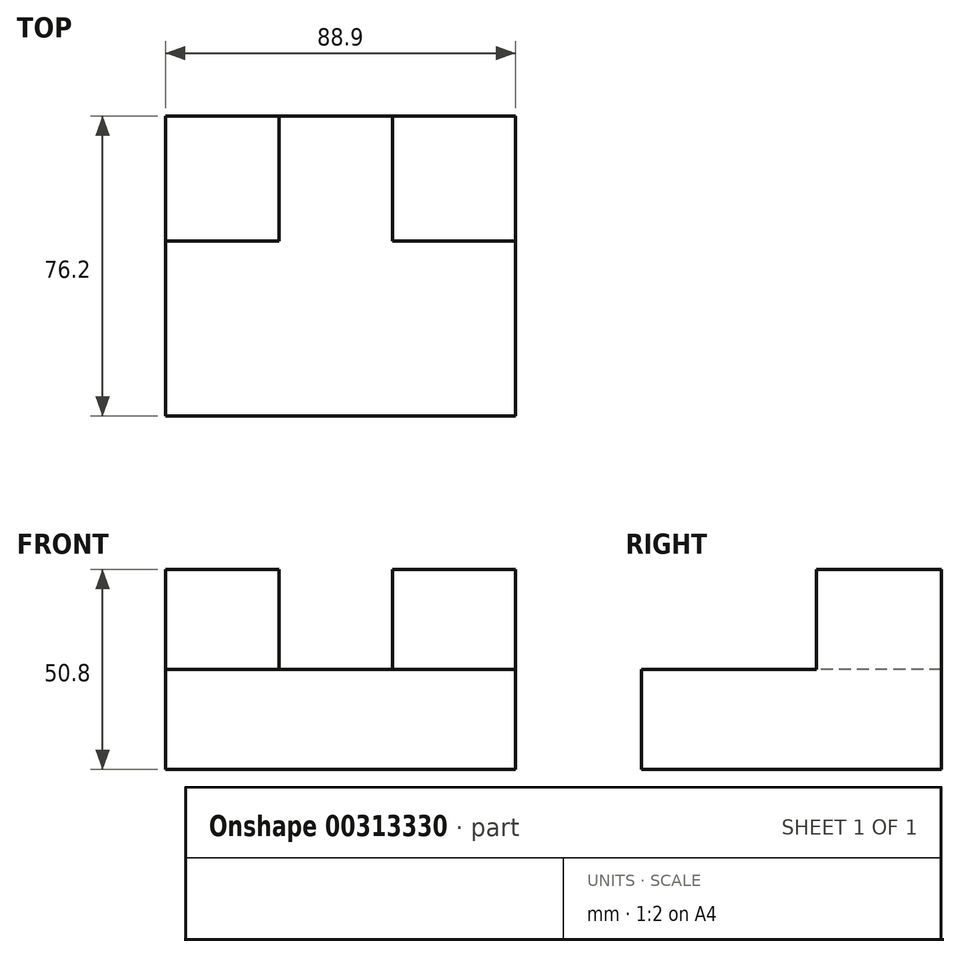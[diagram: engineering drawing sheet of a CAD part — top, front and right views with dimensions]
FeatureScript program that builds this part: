
annotation { "Feature Type Name" : "Feature", "Feature Type Description" : "" }
export const myFeature = defineFeature(function(context is Context, id is Id, definition is map)
    precondition{}
    {
        {
            var Q0;
            Q0=qCreatedBy(makeId("Front.planeOp"),FACE);
            var sketch = newSketch(context, id + "F0", { "sketchPlane" : qUnion([Q0])});
            skLineSegment(sketch, "E0", {"start": v(-64.74, -39.72) * mm, "end": v(24.16, -39.72) * mm});
            skLineSegment(sketch, "E1", {"start": v(24.16, -39.72) * mm, "end": v(24.16, -14.32) * mm});
            skLineSegment(sketch, "E2", {"start": v(24.16, -14.32) * mm, "end": v(-64.74, -14.32) * mm});
            skLineSegment(sketch, "E3", {"start": v(-64.74, -14.32) * mm, "end": v(-64.74, -39.72) * mm});
            skSolve(sketch);
        }
        {
            var Q0;
            Q0=makeQuery(id+"F0.imprint","IMPRINT",FACE,{"disambiguationData":[TD([[makeQuery(id+"F0.imprint","IMPRINT",EDGE,{"derivedFrom":sQuery(id+"F0.wireOp",EDGE,"E0")}),1.0]])]});
            extrude(context, id + "F1", {"entities" : qUnion([Q0]), "depth" : 76.2 * mm});
        }
        {
            var Q0;
            Q0=makeQuery(id+"F1.opExtrude","SWEPT_FACE",FACE,{"disambiguationData":[OSD([sQuery(id+"F0.wireOp",EDGE,"E2")])]});
            var sketch = newSketch(context, id + "F2", { "sketchPlane" : qUnion([Q0])});
            skLineSegment(sketch, "E4", {"start": v(-7.1, 0) * mm, "end": v(-7.1, -31.78) * mm});
            skLineSegment(sketch, "E5", {"start": v(-7.1, -31.78) * mm, "end": v(24.16, -31.78) * mm});
            skSolve(sketch);
        }
        {
            var Q0;
            {var subQ0=sQuery(id+"F2.wireOp",EDGE,"E4");Q0=makeQuery(id+"F2.imprint","IMPRINT",FACE,{"disambiguationData":[TD([[makeQuery(id+"F2.imprint","IMPRINT",EDGE,{"derivedFrom":subQ0}),1.0]])]});}
            extrude(context, id + "F3", {"entities" : qUnion([Q0]), "operationType" : NewBodyOperationType.ADD, "depth" : 25.4 * mm});
        }
        {
            var Q0;
            Q0=makeQuery(id+"F1.opExtrude","SWEPT_FACE",FACE,{"disambiguationData":[OSD([sQuery(id+"F0.wireOp",EDGE,"E2")])]});
            var sketch = newSketch(context, id + "F4", { "sketchPlane" : qUnion([Q0])});
            skLineSegment(sketch, "E6", {"start": v(-35.91, 0) * mm, "end": v(-35.91, -31.78) * mm});
            skLineSegment(sketch, "E7", {"start": v(-35.91, -31.78) * mm, "end": v(-64.74, -31.78) * mm});
            skSolve(sketch);
        }
        {
            var Q0;
            {var subQ0=sQuery(id+"F4.wireOp",EDGE,"E6");Q0=makeQuery(id+"F4.imprint","IMPRINT",FACE,{"disambiguationData":[TD([[makeQuery(id+"F4.imprint","IMPRINT",EDGE,{"derivedFrom":subQ0}),-1.0]])]});}
            extrude(context, id + "F5", {"entities" : qUnion([Q0]), "operationType" : NewBodyOperationType.ADD, "depth" : 25.4 * mm});
        }
    });
